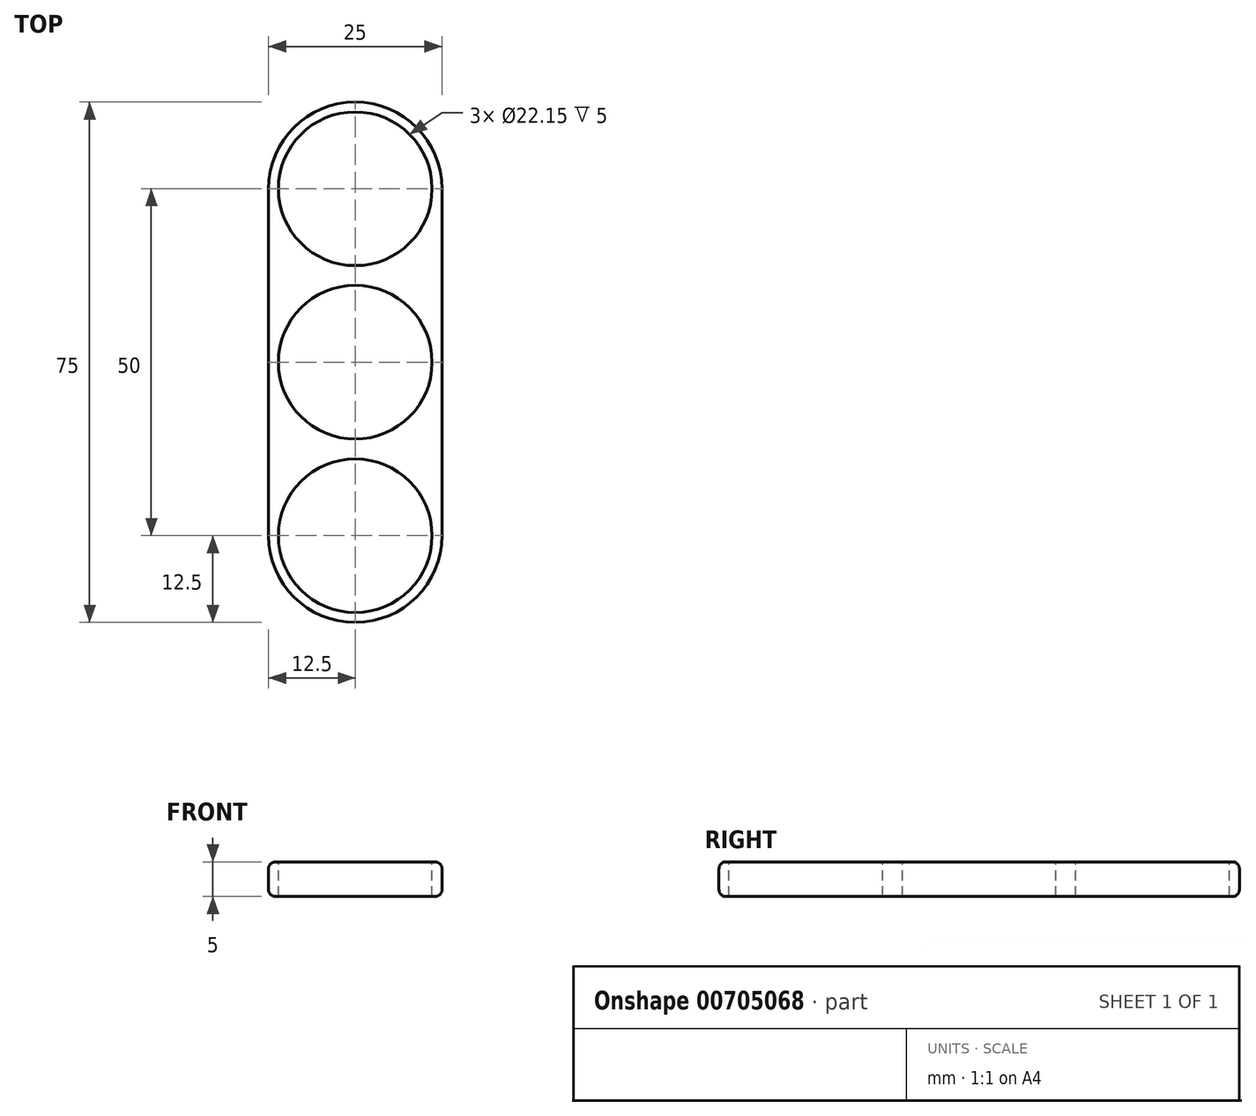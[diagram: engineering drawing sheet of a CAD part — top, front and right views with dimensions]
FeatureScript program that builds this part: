
annotation { "Feature Type Name" : "Feature", "Feature Type Description" : "" }
export const myFeature = defineFeature(function(context is Context, id is Id, definition is map)
    precondition{}
    {
        {
            var Q0;
            Q0=qCreatedBy(makeId("Top.planeOp"),FACE);
            var sketch = newSketch(context, id + "F0", { "sketchPlane" : qUnion([Q0])});
            skCircle(sketch, "E0", {"center": v(0, 0) * mm, "radius": 12.5 * mm});
            skCircle(sketch, "E1", {"center": v(0, 25) * mm, "radius": 12.5 * mm});
            skCircle(sketch, "E2", {"center": v(0, -25) * mm, "radius": 12.5 * mm});
            skLineSegment(sketch, "E3", {"start": v(-12.5, 25) * mm, "end": v(-12.5, -25) * mm});
            skLineSegment(sketch, "E4", {"start": v(-12.5, -25) * mm, "end": v(12.5, -25) * mm});
            skLineSegment(sketch, "E5", {"start": v(12.5, -25) * mm, "end": v(12.5, 25) * mm});
            skLineSegment(sketch, "E6", {"start": v(12.5, 25) * mm, "end": v(-12.5, 25) * mm});
            skSolve(sketch);
        }
        {
            var Q0;
            {var subQ0=sQuery(id+"F0.wireOp",EDGE,"E4");Q0=makeQuery(id+"F0.imprint","IMPRINT",FACE,{"disambiguationData":[TD([[makeQuery(id+"F0.imprint","IMPRINT",EDGE,{"derivedFrom":subQ0}),-1.0]])]});}
            var Q1;
            {var subQ0=sQuery(id+"F0.wireOp",EDGE,"E6");Q1=makeQuery(id+"F0.imprint","IMPRINT",FACE,{"disambiguationData":[TD([[makeQuery(id+"F0.imprint","IMPRINT",EDGE,{"derivedFrom":subQ0}),-1.0]])]});}
            var Q2;
            {var subQ0=sQuery(id+"F0.wireOp",EDGE,"E5");var subQ1=sQuery(id+"F0.wireOp",EDGE,"E0");var subQ2=makeQuery(id+"F0.imprint","INTERSECT",VERTEX,{"derivedFrom":[subQ1,subQ0]});Q2=makeQuery(id+"F0.imprint","IMPRINT",FACE,{"disambiguationData":[TD([[makeQuery(id+"F0.imprint","IMPRINT",EDGE,{"disambiguationData":[TD([[subQ2,-1.0]])],"derivedFrom":subQ1}),-1.0]])]});}
            var Q3;
            {var subQ0=sQuery(id+"F0.wireOp",EDGE,"E3");var subQ1=sQuery(id+"F0.wireOp",EDGE,"E0");var subQ2=makeQuery(id+"F0.imprint","INTERSECT",VERTEX,{"derivedFrom":[subQ1,subQ0]});Q3=makeQuery(id+"F0.imprint","IMPRINT",FACE,{"disambiguationData":[TD([[makeQuery(id+"F0.imprint","IMPRINT",EDGE,{"disambiguationData":[TD([[subQ2,1.0]])],"derivedFrom":subQ1}),-1.0]])]});}
            var Q4;
            {var subQ0=sQuery(id+"F0.wireOp",EDGE,"E3");var subQ1=sQuery(id+"F0.wireOp",EDGE,"E0");var subQ2=makeQuery(id+"F0.imprint","INTERSECT",VERTEX,{"derivedFrom":[subQ1,subQ0]});Q4=makeQuery(id+"F0.imprint","IMPRINT",FACE,{"disambiguationData":[TD([[makeQuery(id+"F0.imprint","IMPRINT",EDGE,{"disambiguationData":[TD([[subQ2,-1.0]])],"derivedFrom":subQ1}),-1.0]])]});}
            var Q5;
            {var subQ0=sQuery(id+"F0.wireOp",EDGE,"E5");var subQ1=sQuery(id+"F0.wireOp",EDGE,"E0");var subQ2=makeQuery(id+"F0.imprint","INTERSECT",VERTEX,{"derivedFrom":[subQ1,subQ0]});Q5=makeQuery(id+"F0.imprint","IMPRINT",FACE,{"disambiguationData":[TD([[makeQuery(id+"F0.imprint","IMPRINT",EDGE,{"disambiguationData":[TD([[subQ2,1.0]])],"derivedFrom":subQ1}),-1.0]])]});}
            var Q6;
            {var subQ0=sQuery(id+"F0.wireOp",EDGE,"E6");Q6=makeQuery(id+"F0.imprint","IMPRINT",FACE,{"disambiguationData":[TD([[makeQuery(id+"F0.imprint","IMPRINT",EDGE,{"derivedFrom":subQ0}),1.0]])]});}
            var Q7;
            {var subQ0=sQuery(id+"F0.wireOp",EDGE,"E4");Q7=makeQuery(id+"F0.imprint","IMPRINT",FACE,{"disambiguationData":[TD([[makeQuery(id+"F0.imprint","IMPRINT",EDGE,{"derivedFrom":subQ0}),1.0]])]});}
            var Q8;
            {var subQ0=sQuery(id+"F0.wireOp",EDGE,"E0");var subQ1=makeQuery(id+"F0.imprint","INTERSECT",VERTEX,{"derivedFrom":[subQ0,sQuery(id+"F0.wireOp",EDGE,"E5")]});Q8=makeQuery(id+"F0.imprint","IMPRINT",FACE,{"disambiguationData":[TD([[makeQuery(id+"F0.imprint","IMPRINT",EDGE,{"disambiguationData":[TD([[subQ1,-1.0]])],"derivedFrom":subQ0}),1.0]])]});}
            extrude(context, id + "F1", {"entities" : qUnion([Q0, Q1, Q2, Q3, Q4, Q5, Q6, Q7, Q8]), "depth" : 5 * mm, "offsetDistance" : 25 * mm});
        }
        {
            var Q0;
            Q0=makeQuery(id+"F1.opExtrude","CAP_FACE",FACE,{"disambiguationData":[OSD([sQuery(id+"F0.wireOp",EDGE,"E1"),sQuery(id+"F0.wireOp",EDGE,"E2"),sQuery(id+"F0.wireOp",EDGE,"E3"),sQuery(id+"F0.wireOp",EDGE,"E5")])],"isStart":false});
            var sketch = newSketch(context, id + "F2", { "sketchPlane" : qUnion([Q0])});
            skCircle(sketch, "E7", {"center": v(0, 25) * mm, "radius": 11.07 * mm});
            skCircle(sketch, "E8", {"center": v(0, 0) * mm, "radius": 11.07 * mm});
            skCircle(sketch, "E9", {"center": v(0, -25) * mm, "radius": 11.07 * mm});
            skSolve(sketch);
        }
        {
            var Q0;
            Q0 = qSketchRegion(id + "F2", true);
            extrude(context, id + "F3", {"entities" : qUnion([Q0]), "operationType" : NewBodyOperationType.REMOVE, "oppositeDirection" : true, "depth" : 25 * mm, "offsetDistance" : 25 * mm});
        }
        {
            var Q0;
            Q0=makeQuery(id+"F1.opExtrude","CAP_EDGE",EDGE,{"disambiguationData":[OSD([sQuery(id+"F0.wireOp",EDGE,"E5")])],"isStart":false});
            var Q1;
            Q1=makeQuery(id+"F1.opExtrude","CAP_EDGE",EDGE,{"disambiguationData":[OSD([sQuery(id+"F0.wireOp",EDGE,"E1")])],"isStart":false});
            var Q2;
            Q2=makeQuery(id+"F1.opExtrude","CAP_EDGE",EDGE,{"disambiguationData":[OSD([sQuery(id+"F0.wireOp",EDGE,"E3")])],"isStart":false});
            var Q3;
            Q3=makeQuery(id+"F1.opExtrude","CAP_EDGE",EDGE,{"disambiguationData":[OSD([sQuery(id+"F0.wireOp",EDGE,"E2")])],"isStart":false});
            var Q4;
            Q4=makeQuery(id+"F1.opExtrude","CAP_EDGE",EDGE,{"disambiguationData":[OSD([sQuery(id+"F0.wireOp",EDGE,"E3")])],"isStart":true});
            var Q5;
            Q5=makeQuery(id+"F1.opExtrude","CAP_EDGE",EDGE,{"disambiguationData":[OSD([sQuery(id+"F0.wireOp",EDGE,"E1")])],"isStart":true});
            var Q6;
            Q6=makeQuery(id+"F1.opExtrude","CAP_EDGE",EDGE,{"disambiguationData":[OSD([sQuery(id+"F0.wireOp",EDGE,"E5")])],"isStart":true});
            var Q7;
            Q7=makeQuery(id+"F1.opExtrude","CAP_EDGE",EDGE,{"disambiguationData":[OSD([sQuery(id+"F0.wireOp",EDGE,"E2")])],"isStart":true});
            fillet(context, id + "F4", {"entities" : qUnion([Q0, Q1, Q2, Q3, Q4, Q5, Q6, Q7]), "radius" : 1 * mm, "tangentPropagation" : true, "allowEdgeOverflow" : false});
        }
    });
